# Revit family: 4630 Mesa Table
name_source: partatom
category: Furniture
revit_build: Autodesk Revit 2017 (Build: 20171027_0315(x64)
units: mm (PartAtom-declared; Revit-internal decimal feet)

## family parameters
Always vertical = Yes
Cut with Voids When Loaded = No
OmniClass Number = 23.40.20.00
OmniClass Title = General Furniture and Specialties
Room Calculation Point = No
Shared = No
Work Plane-Based = No

## types (1)
- 4630 Mesa Table
    Description = With its slim 14 mm tabletop, Mesa is an understated line drawn through the room. The linoleum or laminate tabletop stands in sharp contrast to the soft curves of the aluminium frame and legs.
    Design year = 2013
    Designer = Welling/Ludvik
    Frame = FF Aluminium White
    Height = 73 cm
    Item No. = 4630
    Length = 300 cm
    Manufacturer = Fredericia Furniture A/S
    Model = Mesa Table
    Table Top = FF Linoleum White
    URL = https://www.fredericia.com
    Variations Dimensions = Available in special sizes by request
    Variations Frame = Available in black or white
    Variations Tabletop = Available in black linoleum, white nano laminate or oak veneer lacquered
    Weight = 63 kg
    Width = 120 cm

## geometry (parser evidence)
native form markers: Sweep x3
no freeform markers — native parametric forms only
